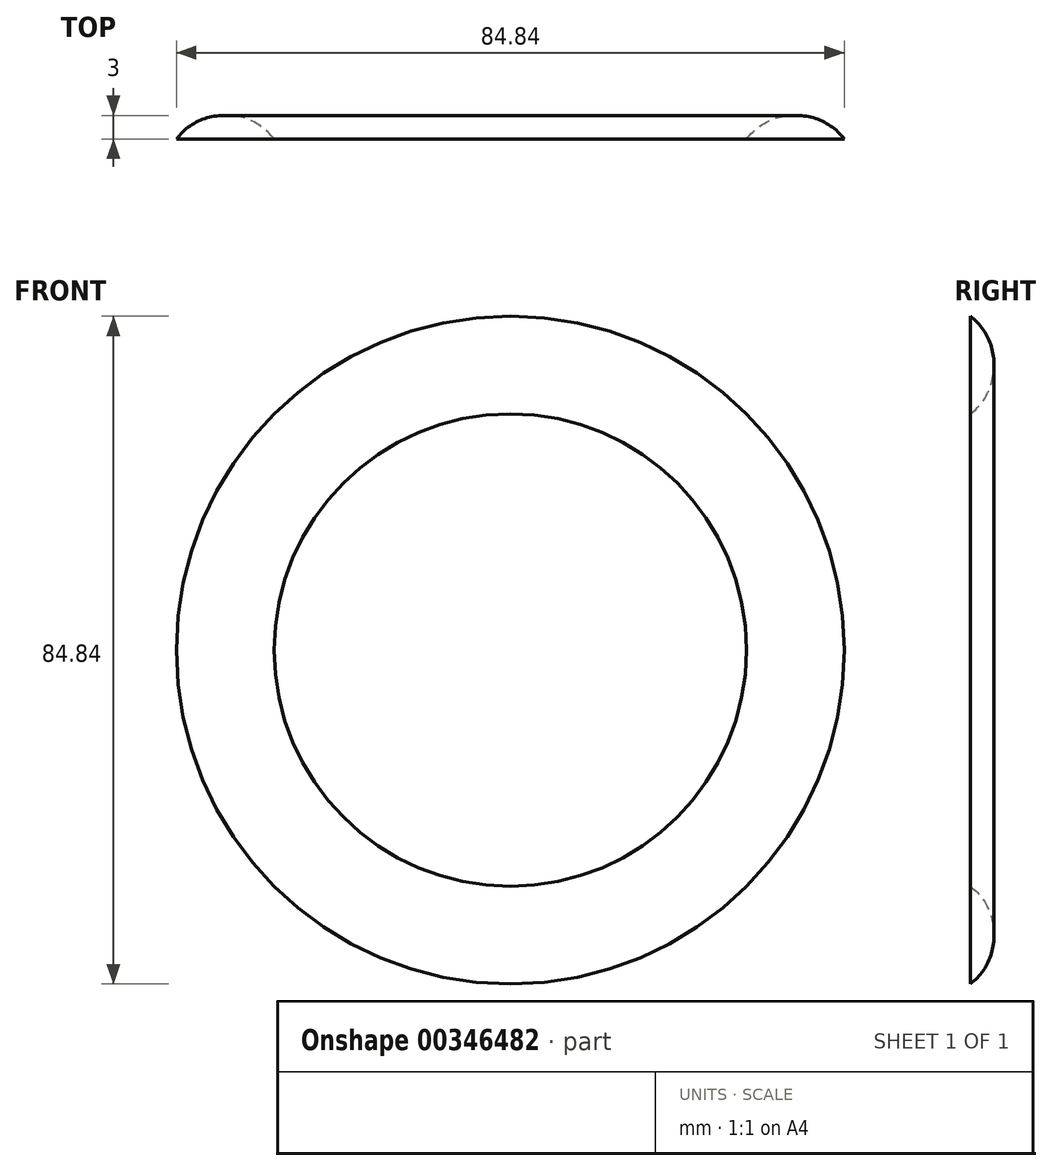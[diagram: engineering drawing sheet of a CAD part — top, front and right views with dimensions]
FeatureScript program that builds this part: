
annotation { "Feature Type Name" : "Feature", "Feature Type Description" : "" }
export const myFeature = defineFeature(function(context is Context, id is Id, definition is map)
    precondition{}
    {
        {
            var Q0;
            Q0=qCreatedBy(makeId("Front.planeOp"),FACE);
            var sketch = newSketch(context, id + "F0", { "sketchPlane" : qUnion([Q0])});
            skCircle(sketch, "E0", {"center": v(0, 0) * mm, "radius": 30 * mm});
            skCircle(sketch, "E1", {"center": v(0, 0) * mm, "radius": 42.42 * mm});
            skSolve(sketch);
        }
        {
            var Q0;
            Q0 = qSketchRegion(id + "F0", true);
            extrude(context, id + "F1", {"entities" : qUnion([Q0]), "depth" : 3 * mm, "offsetDistance" : 25 * mm});
        }
        {
            var Q0;
            Q0=makeQuery(id+"F1.opExtrude","CAP_EDGE",EDGE,{"disambiguationData":[OSD([sQuery(id+"F0.wireOp",EDGE,"E0")])],"isStart":true});
            var Q1;
            Q1=makeQuery(id+"F1.opExtrude","CAP_EDGE",EDGE,{"disambiguationData":[OSD([sQuery(id+"F0.wireOp",EDGE,"E1")])],"isStart":true});
            fillet(context, id + "F2", {"entities" : qUnion([Q0, Q1]), "radius" : 7.5 * mm, "tangentPropagation" : true, "allowEdgeOverflow" : false});
        }
    });
